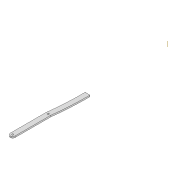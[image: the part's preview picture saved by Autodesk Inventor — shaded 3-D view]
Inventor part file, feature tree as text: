
AUTODESK INVENTOR PART (.ipt)
format: ipt  version: 2022 (Build 260153000, 153)  size: 108,032 bytes
history: native  units: mm
features: extrude x2, sketch x2, other x1
ambient origin geometry x8: Origin, YZ Plane, XZ Plane, XY Plane, X Axis, Y Axis, Z Axis, Center Point
bodies: Solid1 (feature_tree)
feature tree (5):
  extrude  "Extrusion1"  Depth=3.3mm
  other  "Work Axis3"
  extrude  "Extrusion2"  Depth=600.0mm
  sketch  "Sketch1"  dims[d0=3.3mm d1=3.3mm]
  sketch  "Sketch2"  dims[d2=10.0mm d3=322.934mm d4=3.3mm d5=74.182mm d6=3.0mm d7=0.0mm d8=3.3mm d9=218.733mm d12=600.0mm d13=600.0mm d14=100.0mm d15=0.0mm]
